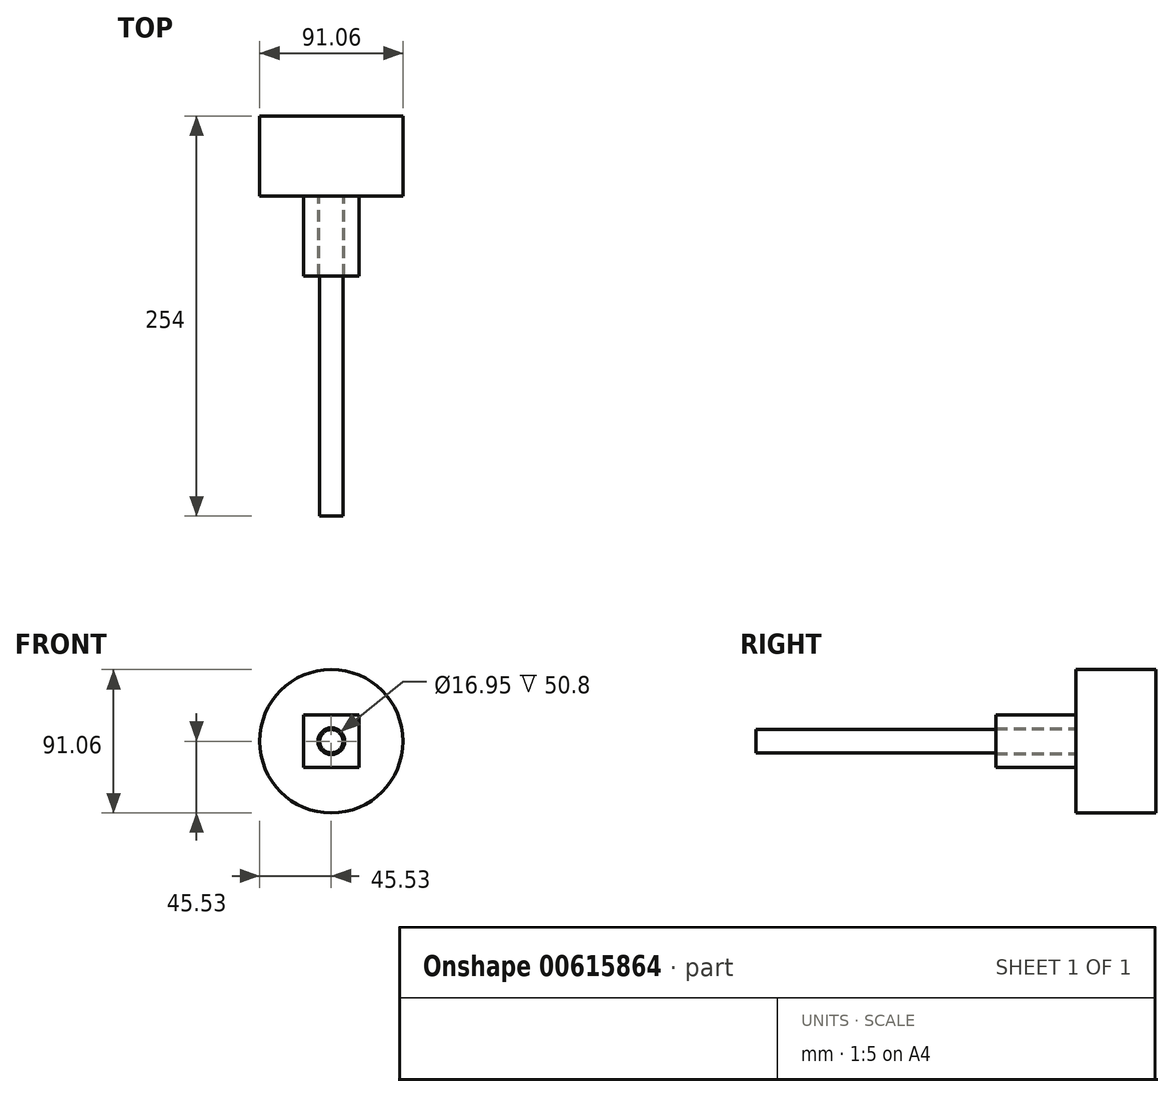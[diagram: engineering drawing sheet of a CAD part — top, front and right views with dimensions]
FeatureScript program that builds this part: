
annotation { "Feature Type Name" : "Feature", "Feature Type Description" : "" }
export const myFeature = defineFeature(function(context is Context, id is Id, definition is map)
    precondition{}
    {
        {
            var Q0;
            Q0=qCreatedBy(makeId("Front.planeOp"),FACE);
            var sketch = newSketch(context, id + "F0", { "sketchPlane" : qUnion([Q0])});
            skCircle(sketch, "E0", {"center": v(0, 0) * mm, "radius": 41.05 * mm});
            skLineSegment(sketch, "E1.bottom", {"start": v(17.56, 16.63) * mm, "end": v(-17.56, 16.63) * mm});
            skLineSegment(sketch, "E1.top", {"start": v(17.56, -16.63) * mm, "end": v(-17.56, -16.63) * mm});
            skLineSegment(sketch, "E1.left", {"start": v(17.56, 16.63) * mm, "end": v(17.56, -16.63) * mm});
            skLineSegment(sketch, "E1.right", {"start": v(-17.56, 16.63) * mm, "end": v(-17.56, -16.63) * mm});
            skCircle(sketch, "E2", {"center": v(0, 0) * mm, "radius": 8.48 * mm});
            skSolve(sketch);
        }
        {
            var Q0;
            Q0=makeQuery(id+"F0.imprint","IMPRINT",FACE,{"disambiguationData":[TD([[makeQuery(id+"F0.imprint","IMPRINT",EDGE,{"derivedFrom":sQuery(id+"F0.wireOp",EDGE,"E1.bottom")}),1.0]])]});
            extrude(context, id + "F1", {"entities" : qUnion([Q0]), "depth" : 101.6 * mm, "offsetDistance" : 25.4 * mm});
        }
        {
            var Q0;
            Q0=qCreatedBy(makeId("Front.planeOp"),FACE);
            var sketch = newSketch(context, id + "F2", { "sketchPlane" : qUnion([Q0])});
            skCircle(sketch, "E3", {"center": v(0, 0) * mm, "radius": 45.53 * mm});
            skSolve(sketch);
        }
        {
            var Q0;
            Q0 = qSketchRegion(id + "F2", true);
            extrude(context, id + "F3", {"entities" : qUnion([Q0]), "operationType" : NewBodyOperationType.ADD, "depth" : 50.8 * mm, "offsetDistance" : 25.4 * mm});
        }
        {
            var Q0;
            Q0=qCreatedBy(makeId("Front.planeOp"),FACE);
            var sketch = newSketch(context, id + "F4", { "sketchPlane" : qUnion([Q0])});
            skCircle(sketch, "E4", {"center": v(0, 0) * mm, "radius": 7.39 * mm});
            skSolve(sketch);
        }
        {
            var Q0;
            Q0 = qSketchRegion(id + "F4", true);
            extrude(context, id + "F5", {"entities" : qUnion([Q0]), "operationType" : NewBodyOperationType.ADD, "depth" : 254 * mm, "offsetDistance" : 25.4 * mm});
        }
    });
